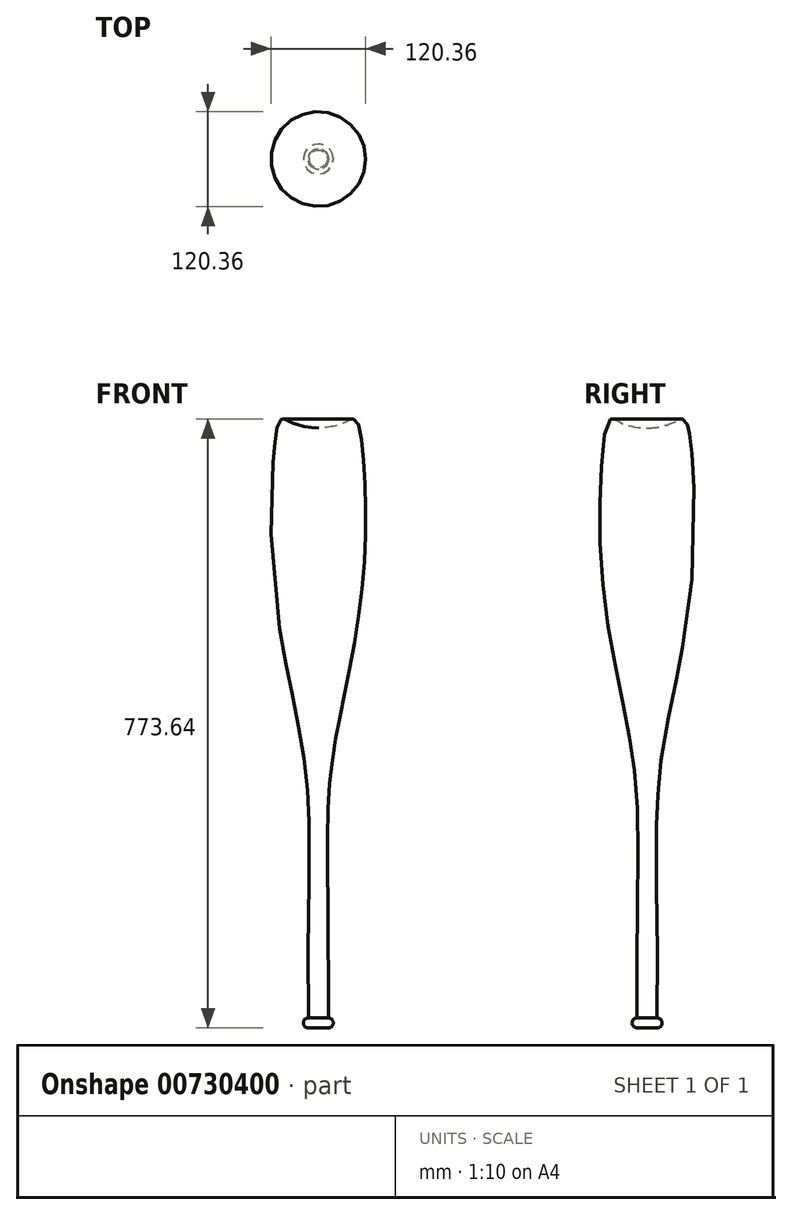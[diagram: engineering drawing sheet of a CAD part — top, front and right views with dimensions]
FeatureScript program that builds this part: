
annotation { "Feature Type Name" : "Feature", "Feature Type Description" : "" }
export const myFeature = defineFeature(function(context is Context, id is Id, definition is map)
    precondition{}
    {
        {
            var Q0;
            Q0=qCreatedBy(makeId("Front.planeOp"),FACE);
            var sketch = newSketch(context, id + "F0", { "sketchPlane" : qUnion([Q0])});
            skLineSegment(sketch, "E0", {"start": v(0, 464.13) * mm, "end": v(0, -297.87) * mm});
            skLineSegment(sketch, "E1", {"start": v(0, -297.87) * mm, "end": v(12.7, -297.87) * mm});
            skArc(sketch, "E2", {"start": v(12.7, -297.87) * mm, "mid": v(19.05, -291.52) * mm, "end": v(12.7, -285.17) * mm});
            skFitSpline(sketch, "E3", {"points": [v(12.7, -285.17) * mm, v(12.84, -11.55) * mm, v(29.6, 108) * mm, v(56.3, 264.72) * mm, v(57.78, 417.37) * mm, v(46.98, 475.15) * mm, v(0, 464.13) * mm], "startDerivative": vector(19.17, 1266.71) * mm, "endDerivative": vector(-954.17, -24.96) * mm});
            skSolve(sketch);
        }
        {
            var Q0;
            Q0=makeQuery(id+"F0.imprint","IMPRINT",FACE,{"disambiguationData":[TD([[makeQuery(id+"F0.imprint","IMPRINT",EDGE,{"derivedFrom":sQuery(id+"F0.wireOp",EDGE,"E0")}),1.0]])]});
            var Q1;
            Q1=sQuery(id+"F0.wireOp",EDGE,"E0");
            revolve(context, id + "F1", {"surfaceOperationType" : NewSurfaceOperationType.NEW, "entities" : qUnion([Q0]), "axis" : qUnion([Q1]), "revolveType" : RevolveType.FULL});
        }
    });
